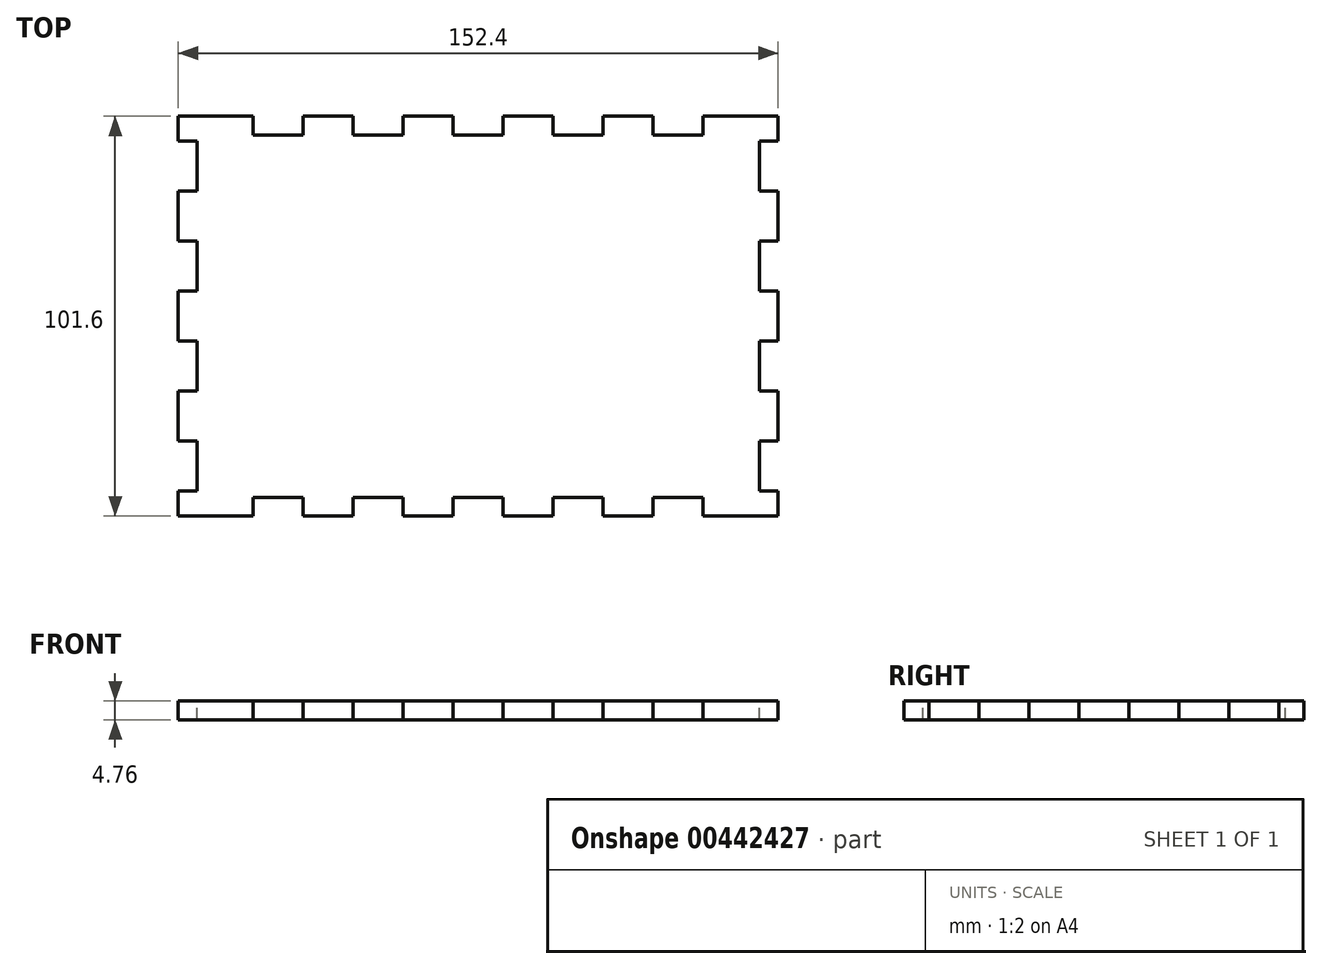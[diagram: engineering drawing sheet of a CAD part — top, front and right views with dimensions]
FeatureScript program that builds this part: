
annotation { "Feature Type Name" : "Feature", "Feature Type Description" : "" }
export const myFeature = defineFeature(function(context is Context, id is Id, definition is map)
    precondition{}
    {
        {
            var Q0;
            Q0=qCreatedBy(makeId("Top.planeOp"),FACE);
            var sketch = newSketch(context, id + "F0", { "sketchPlane" : qUnion([Q0])});
            skLineSegment(sketch, "E0.bottom", {"start": v(-76.2, 50.8) * mm, "end": v(76.2, 50.8) * mm});
            skLineSegment(sketch, "E0.top", {"start": v(-76.2, -50.8) * mm, "end": v(76.2, -50.8) * mm});
            skLineSegment(sketch, "E0.left", {"start": v(-76.2, 50.8) * mm, "end": v(-76.2, -50.8) * mm});
            skLineSegment(sketch, "E0.right", {"start": v(76.2, 50.8) * mm, "end": v(76.2, -50.8) * mm});
            skPoint(sketch, "E0.middle", {"position": v(0, 0) * mm});
            skSolve(sketch);
        }
        {
            var Q0;
            Q0 = qSketchRegion(id + "F0", true);
            extrude(context, id + "F1", {"entities" : qUnion([Q0]), "depth" : 4.76 * mm});
        }
        {
            var Q0;
            Q0=makeQuery(id+"F1.opExtrude","CAP_FACE",FACE,{"disambiguationData":[OSD([sQuery(id+"F0.wireOp",EDGE,"E0.bottom"),sQuery(id+"F0.wireOp",EDGE,"E0.top"),sQuery(id+"F0.wireOp",EDGE,"E0.left"),sQuery(id+"F0.wireOp",EDGE,"E0.right")])],"isStart":false});
            var sketch = newSketch(context, id + "F2", { "sketchPlane" : qUnion([Q0])});
            skLineSegment(sketch, "E1", {"start": v(-57.15, 50.8) * mm, "end": v(-57.15, 46.04) * mm});
            skLineSegment(sketch, "E2", {"start": v(-57.15, 46.04) * mm, "end": v(-44.45, 46.04) * mm});
            skLineSegment(sketch, "E3", {"start": v(-44.45, 46.04) * mm, "end": v(-44.45, 50.8) * mm});
            skLineSegment(sketch, "E4.1.0.0", {"start": v(-31.75, 50.8) * mm, "end": v(-31.75, 46.04) * mm});
            skLineSegment(sketch, "E4.1.0.1", {"start": v(-31.75, 46.04) * mm, "end": v(-19.05, 46.04) * mm});
            skLineSegment(sketch, "E4.1.0.2", {"start": v(-19.05, 46.04) * mm, "end": v(-19.05, 50.8) * mm});
            skLineSegment(sketch, "E4.2.0.0", {"start": v(-6.35, 50.8) * mm, "end": v(-6.35, 46.04) * mm});
            skLineSegment(sketch, "E4.2.0.1", {"start": v(-6.35, 46.04) * mm, "end": v(6.35, 46.04) * mm});
            skLineSegment(sketch, "E4.2.0.2", {"start": v(6.35, 46.04) * mm, "end": v(6.35, 50.8) * mm});
            skLineSegment(sketch, "E4.direction1", {"start": v(-57.15, 46.04) * mm, "end": v(-31.75, 46.04) * mm, "construction": true});
            skLineSegment(sketch, "E5", {"start": v(0, 0) * mm, "end": v(11.05, 0) * mm, "construction": true});
            skLineSegment(sketch, "E6", {"start": v(-57.15, 50.8) * mm, "end": v(-44.45, 50.8) * mm});
            skLineSegment(sketch, "E7", {"start": v(-31.75, 50.8) * mm, "end": v(-19.05, 50.8) * mm});
            skLineSegment(sketch, "E8", {"start": v(-6.35, 50.8) * mm, "end": v(6.35, 50.8) * mm});
            skLineSegment(sketch, "E9", {"start": v(0, 0) * mm, "end": v(0, 4.96) * mm, "construction": true});
            skLineSegment(sketch, "E10", {"start": v(-76.2, -44.45) * mm, "end": v(-71.44, -44.45) * mm});
            skLineSegment(sketch, "E11", {"start": v(-71.44, -44.45) * mm, "end": v(-71.44, -31.75) * mm});
            skLineSegment(sketch, "E12", {"start": v(-71.44, -31.75) * mm, "end": v(-76.2, -31.75) * mm});
            skLineSegment(sketch, "E13.0.1.0", {"start": v(-71.44, -6.35) * mm, "end": v(-76.2, -6.35) * mm});
            skLineSegment(sketch, "E13.0.1.1", {"start": v(-76.2, -19.05) * mm, "end": v(-71.44, -19.05) * mm});
            skLineSegment(sketch, "E13.0.1.2", {"start": v(-71.44, -19.05) * mm, "end": v(-71.44, -6.35) * mm});
            skLineSegment(sketch, "E13.0.2.0", {"start": v(-71.44, 19.05) * mm, "end": v(-76.2, 19.05) * mm});
            skLineSegment(sketch, "E13.0.2.1", {"start": v(-76.2, 6.35) * mm, "end": v(-71.44, 6.35) * mm});
            skLineSegment(sketch, "E13.0.2.2", {"start": v(-71.44, 6.35) * mm, "end": v(-71.44, 19.05) * mm});
            skLineSegment(sketch, "E13.direction1", {"start": v(-76.2, -31.75) * mm, "end": v(-25.4, -31.75) * mm, "construction": true});
            skLineSegment(sketch, "E13.direction2", {"start": v(-76.2, -31.75) * mm, "end": v(-76.2, -6.35) * mm, "construction": true});
            skLineSegment(sketch, "E14", {"start": v(-76.2, 6.35) * mm, "end": v(-76.2, 19.05) * mm});
            skLineSegment(sketch, "E15", {"start": v(-76.2, -6.35) * mm, "end": v(-76.2, -19.05) * mm});
            skLineSegment(sketch, "E16", {"start": v(-76.2, -31.75) * mm, "end": v(-76.2, -44.45) * mm});
            skLineSegment(sketch, "E17.MirrorCS", {"start": v(-57.15, -50.8) * mm, "end": v(-57.15, -46.04) * mm});
            skLineSegment(sketch, "E18.MirrorCS", {"start": v(-57.15, -50.8) * mm, "end": v(-44.45, -50.8) * mm});
            skLineSegment(sketch, "E19.MirrorCS", {"start": v(-57.15, -46.04) * mm, "end": v(-31.75, -46.04) * mm, "construction": true});
            skLineSegment(sketch, "E20.MirrorCS", {"start": v(-44.45, -46.04) * mm, "end": v(-44.45, -50.8) * mm});
            skLineSegment(sketch, "E21.MirrorCS", {"start": v(-31.75, -50.8) * mm, "end": v(-31.75, -46.04) * mm});
            skLineSegment(sketch, "E22.MirrorCS", {"start": v(-31.75, -50.8) * mm, "end": v(-19.05, -50.8) * mm});
            skLineSegment(sketch, "E23.MirrorCS", {"start": v(-31.75, -46.04) * mm, "end": v(-19.05, -46.04) * mm});
            skLineSegment(sketch, "E24.MirrorCS", {"start": v(-19.05, -46.04) * mm, "end": v(-19.05, -50.8) * mm});
            skLineSegment(sketch, "E25.MirrorCS", {"start": v(-6.35, -50.8) * mm, "end": v(-6.35, -46.04) * mm});
            skLineSegment(sketch, "E26.MirrorCS", {"start": v(-6.35, -50.8) * mm, "end": v(6.35, -50.8) * mm});
            skLineSegment(sketch, "E27.MirrorCS", {"start": v(-6.35, -46.04) * mm, "end": v(6.35, -46.04) * mm});
            skLineSegment(sketch, "E28.MirrorCS", {"start": v(6.35, -46.04) * mm, "end": v(6.35, -50.8) * mm});
            skLineSegment(sketch, "E29", {"start": v(-57.15, -46.04) * mm, "end": v(-44.45, -46.04) * mm});
            skLineSegment(sketch, "E30.MirrorCS", {"start": v(71.44, 19.05) * mm, "end": v(76.2, 19.05) * mm});
            skLineSegment(sketch, "E31.MirrorCS", {"start": v(76.2, 6.35) * mm, "end": v(76.2, 19.05) * mm});
            skLineSegment(sketch, "E32.MirrorCS", {"start": v(76.2, 6.35) * mm, "end": v(71.44, 6.35) * mm});
            skLineSegment(sketch, "E33.MirrorCS", {"start": v(71.44, 6.35) * mm, "end": v(71.44, 19.05) * mm});
            skLineSegment(sketch, "E34.MirrorCS", {"start": v(71.44, -6.35) * mm, "end": v(76.2, -6.35) * mm});
            skLineSegment(sketch, "E35.MirrorCS", {"start": v(76.2, -31.75) * mm, "end": v(76.2, -6.35) * mm, "construction": true});
            skLineSegment(sketch, "E36.MirrorCS", {"start": v(76.2, -19.05) * mm, "end": v(71.44, -19.05) * mm});
            skLineSegment(sketch, "E37.MirrorCS", {"start": v(71.44, -19.05) * mm, "end": v(71.44, -6.35) * mm});
            skLineSegment(sketch, "E38.MirrorCS", {"start": v(71.44, -44.45) * mm, "end": v(71.44, -31.75) * mm});
            skLineSegment(sketch, "E39.MirrorCS", {"start": v(76.2, -44.45) * mm, "end": v(71.44, -44.45) * mm});
            skLineSegment(sketch, "E40.MirrorCS", {"start": v(76.2, -31.75) * mm, "end": v(76.2, -44.45) * mm});
            skLineSegment(sketch, "E41", {"start": v(71.44, -31.75) * mm, "end": v(76.2, -31.75) * mm});
            skLineSegment(sketch, "E42", {"start": v(76.2, -19.05) * mm, "end": v(76.2, -6.35) * mm});
            skLineSegment(sketch, "E43.0.0.3", {"start": v(-71.44, 44.45) * mm, "end": v(-76.2, 44.45) * mm});
            skLineSegment(sketch, "E43.3.0.3", {"start": v(-76.2, 31.75) * mm, "end": v(-71.44, 31.75) * mm});
            skLineSegment(sketch, "E43.6.0.3", {"start": v(-71.44, 31.75) * mm, "end": v(-71.44, 44.45) * mm});
            skLineSegment(sketch, "E44.1.0.0", {"start": v(19.05, 50.8) * mm, "end": v(19.05, 46.04) * mm});
            skLineSegment(sketch, "E44.1.0.1", {"start": v(19.05, 50.8) * mm, "end": v(31.75, 50.8) * mm});
            skLineSegment(sketch, "E44.1.0.2", {"start": v(19.05, 46.04) * mm, "end": v(31.75, 46.04) * mm});
            skLineSegment(sketch, "E44.1.0.3", {"start": v(31.75, 46.04) * mm, "end": v(31.75, 50.8) * mm});
            skLineSegment(sketch, "E44.2.0.0", {"start": v(44.45, 50.8) * mm, "end": v(44.45, 46.04) * mm});
            skLineSegment(sketch, "E44.2.0.1", {"start": v(44.45, 50.8) * mm, "end": v(57.15, 50.8) * mm});
            skLineSegment(sketch, "E44.2.0.2", {"start": v(44.45, 46.04) * mm, "end": v(57.15, 46.04) * mm});
            skLineSegment(sketch, "E44.2.0.3", {"start": v(57.15, 46.04) * mm, "end": v(57.15, 50.8) * mm});
            skLineSegment(sketch, "E44.direction1", {"start": v(-6.35, 46.04) * mm, "end": v(19.05, 46.04) * mm, "construction": true});
            skLineSegment(sketch, "E45.MirrorCS", {"start": v(19.05, -50.8) * mm, "end": v(31.75, -50.8) * mm});
            skLineSegment(sketch, "E46.MirrorCS", {"start": v(19.05, -50.8) * mm, "end": v(19.05, -46.04) * mm});
            skLineSegment(sketch, "E47.MirrorCS", {"start": v(19.05, -46.04) * mm, "end": v(31.75, -46.04) * mm});
            skLineSegment(sketch, "E48.MirrorCS", {"start": v(31.75, -46.04) * mm, "end": v(31.75, -50.8) * mm});
            skLineSegment(sketch, "E49.MirrorCS", {"start": v(44.45, -50.8) * mm, "end": v(57.15, -50.8) * mm});
            skLineSegment(sketch, "E50.MirrorCS", {"start": v(44.45, -50.8) * mm, "end": v(44.45, -46.04) * mm});
            skLineSegment(sketch, "E51.MirrorCS", {"start": v(44.45, -46.04) * mm, "end": v(57.15, -46.04) * mm});
            skLineSegment(sketch, "E52.MirrorCS", {"start": v(57.15, -46.04) * mm, "end": v(57.15, -50.8) * mm});
            skLineSegment(sketch, "E53.MirrorCS", {"start": v(71.44, 44.45) * mm, "end": v(76.2, 44.45) * mm});
            skLineSegment(sketch, "E54.MirrorCS", {"start": v(71.44, 31.75) * mm, "end": v(71.44, 44.45) * mm});
            skLineSegment(sketch, "E55.MirrorCS", {"start": v(76.2, 31.75) * mm, "end": v(71.44, 31.75) * mm});
            skLineSegment(sketch, "E56", {"start": v(-76.2, 31.75) * mm, "end": v(-76.2, 44.45) * mm});
            skLineSegment(sketch, "E57", {"start": v(76.2, 31.75) * mm, "end": v(76.2, 44.45) * mm});
            skSolve(sketch);
        }
        {
            var Q0;
            Q0 = qSketchRegion(id + "F2", true);
            extrude(context, id + "F3", {"entities" : qUnion([Q0]), "operationType" : NewBodyOperationType.REMOVE, "oppositeDirection" : true, "depth" : 25.4 * mm});
        }
    });
